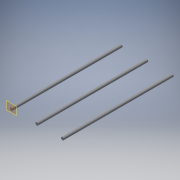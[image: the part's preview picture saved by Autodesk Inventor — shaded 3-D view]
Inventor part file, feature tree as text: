
AUTODESK INVENTOR PART (.ipt)
format: ipt  version: 2016 (Build 200138000, 138)  size: 93,696 bytes
history: native  units: in
note: dims shown in document units (in); Inventor stores cm internally (conversion verified against a paired STEP export)
features: reference x3, plane x2, sketch x1, extrude x1
ambient origin geometry x8: Origin, YZ Plane, XZ Plane, XY Plane, X Axis, Y Axis, Z Axis, Center Point
bodies: Solid1 (feature_tree)
feature tree (7):
  plane  "Work Plane1"
  sketch  "Sketch1"  dims[d0=0.315in d1=1.0in d2=0.0in]
  plane  "Work Plane2"
  extrude  "Extrusion1"  Depth=1.0in TaperAngle=0.0deg
  reference  "Reference1"
  reference  "Reference2"
  reference  "Reference3"
